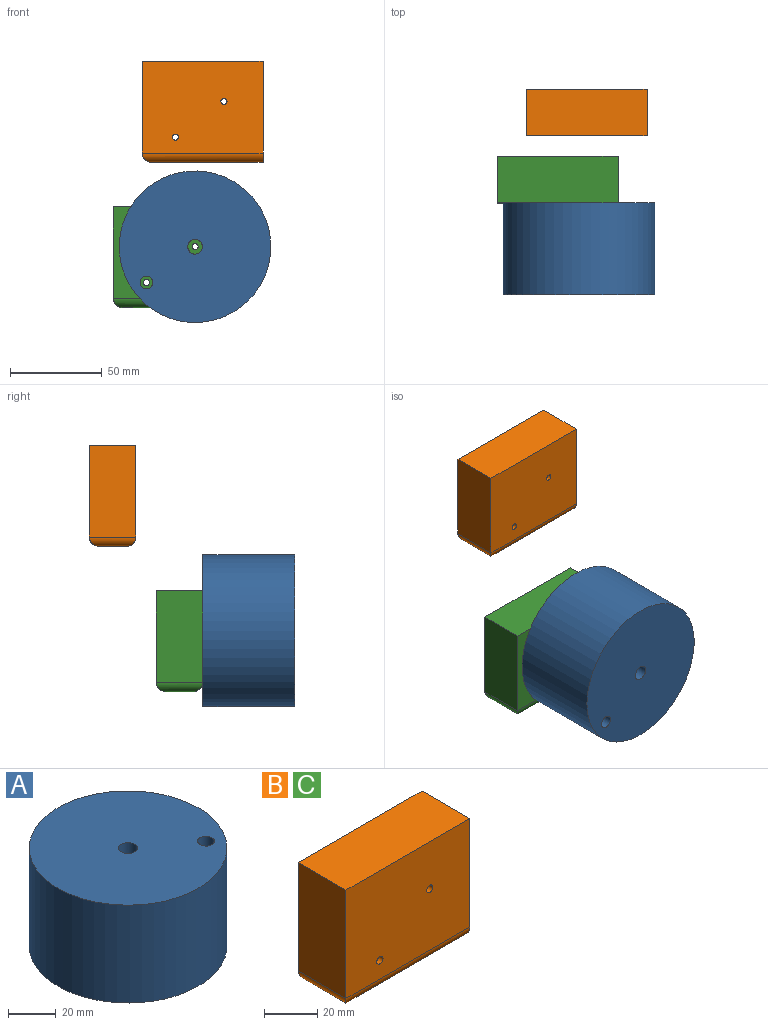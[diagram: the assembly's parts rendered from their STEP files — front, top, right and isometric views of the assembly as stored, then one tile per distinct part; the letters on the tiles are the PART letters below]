
ASSEMBLY  parts=3 mates=1
PART A: 5 faces, bbox 82.6x82.6x50 mm
  f0: cylinder r=41.29mm len=82.59mm, axis (0,0,-1), area 12972.6mm2, adj f1,f2
  f1: plane 82.59x82.59mm, normal (0,0,1), area 5268mm2, adj f0,f3,f4
  f2: plane 82.59x82.59mm, normal (0,0,-1), area 5268mm2, adj f0,f3,f4
  f3: cylinder r=4mm len=50mm, axis (0,0,-1), area 1256.6mm2, adj f1,f2
  f4: cylinder r=3.5mm len=50mm, axis (0,0,1), area 1099.6mm2, adj f1,f2
PART B: 11 faces, bbox 65.8x25.4x54.9 mm
  f0: plane 49.86x25.4mm, normal (-1,0,0), area 1266.4mm2, adj f3,f4,f5,f8
  f1: plane 60.82x15.4mm, normal (0,0,-1), area 936.6mm2, adj f2,f6,f7,f8
  f2: plane 54.86x25.4mm, normal (1,0,0), area 1382.7mm2, adj f1,f3,f4,f5,f6,f7
  f3: plane 65.82x25.4mm, normal (0,0,1), area 1671.8mm2, adj f0,f2,f4,f5
  f4: plane 65.82x49.86mm, normal (0,-1,0), area 3264.6mm2, adj f0,f2,f3,f6,f9,f10
  f5: plane 65.82x49.86mm, normal (0,1,0), area 3264.6mm2, adj f0,f2,f3,f7,f9,f10
  f6: cylinder r=5mm len=65.82mm, axis (-1,0,0), area 502.7mm2, adj f1,f2,f4,f8
  f7: cylinder r=5mm len=65.82mm, axis (1,0,0), area 502.7mm2, adj f1,f2,f5,f8
  f8: cylinder r=5mm len=25.4mm, axis (0,-1,0), area 171mm2, adj f0,f1,f6,f7
  f9: cylinder r=1.65mm len=25.4mm, axis (0,-1,0), area 263.3mm2, adj f4,f5
  f10: cylinder r=1.65mm len=25.4mm, axis (0,-1,0), area 263.3mm2, adj f4,f5
PART C: same geometry as B
PLACE A rot(axis=(0,0.71,0.71),180deg) t=(-64.22,-82.95,-55.57)mm
PLACE B t=(17.13,28.9,19.82)mm
PLACE C t=(1.37,-7.55,-59.39)mm
MATE planar A.f1 <-> C.f4  axis (0,1,0) through (-64.02,-32.95,-55.43)mm
